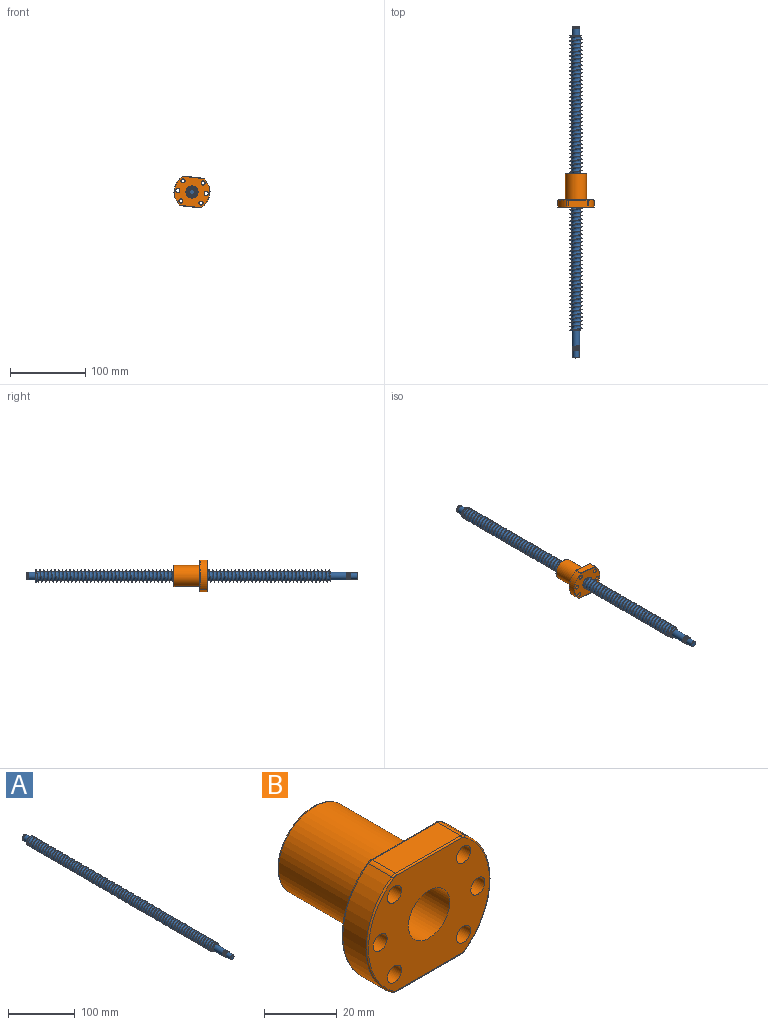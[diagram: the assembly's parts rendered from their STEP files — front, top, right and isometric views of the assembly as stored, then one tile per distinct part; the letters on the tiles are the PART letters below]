
ASSEMBLY  parts=2 mates=1
PART A: 29 faces, bbox 30.7x442.9x26.7 mm
  f0: cylinder r=5mm len=21mm, axis (0,1,0), area 629.1mm2, adj f1,f8,f9,f10,f18
  f1: cylinder r=5mm len=10mm, axis (0,1,0), area 1.6mm2, adj f0,f2,f9,f10
  f2: cylinder r=5mm len=10mm, axis (0,1,0), area 1.6mm2, adj f1,f3,f9,f10
  f3: cylinder r=5mm len=10mm, axis (0,1,0), area 1.6mm2, adj f2,f4,f9,f10
  f4: cylinder r=5mm len=10mm, axis (0,1,0), area 1.6mm2, adj f3,f5,f9,f10
  f5: cylinder r=5mm len=1.58mm, axis (0,1,0), area 0mm2, adj f4,f7,f9
  f6: plane 9.16x8.89mm, normal (0,-1,0), area 11.7mm2, adj f7,f9,f10,f20
  f7: cone r=4.5mm half-angle=45deg, axis (0,1,0), area 7mm2, adj f5,f6,f9,f10
  f8: plane 0.95x0.82mm, normal (-1,0,0), area 0.4mm2, adj f0,f9,f10
  f9: bspline ~11.55x10mm, area 140.3mm2, adj f0,f1,f2,f3,f4,f5,f6,f7
  f10: bspline ~11.55x10mm, area 153.7mm2, adj f0,f1,f2,f3,f4,f6,f7,f8
  f11: bspline ~399.07x29.85mm, area 24636.7mm2, adj f12,f13,f14,f15,f18,f19
  f12: plane 5.62x3.2mm, normal (-0.31,0,-0.95), area 9mm2, adj f11,f15,f19
  f13: cone r=7.03mm half-angle=45deg, axis (0,1,0), area 3.3mm2, adj f11,f18
  f14: cone r=7.03mm half-angle=45deg, axis (0,1,0), area 0.1mm2, adj f11,f19
  f15: cone r=8.02mm half-angle=45deg, axis (0,-1,0), area 60.9mm2, adj f11,f12,f17,f19
  f16: cylinder r=5mm len=10mm, axis (0,-1,0), area 282.7mm2, adj f17,f24
  f17: plane 14.05x14.05mm, normal (0,1,0), area 76.5mm2, adj f15,f16
  f18: plane 12.61x11.89mm, normal (0,-1,0), area 38.8mm2, adj f0,f11,f13
  f19: cylinder r=8.02mm len=392mm, axis (0,1,0), area 8085.4mm2, adj f11,f12,f14,f15
  f20: cylinder r=4mm len=10mm, axis (0,1,0), area 251.3mm2, adj f6,f22
  f21: plane 7x7mm, normal (0,-1,0), area 38.5mm2, adj f22
  f22: cone r=3.5mm half-angle=45deg, axis (0,1,0), area 16.7mm2, adj f20,f21
  f23: plane 10x10mm, normal (0,-1,0), area 6.2mm2, adj f25,f28
  f24: plane 10x10mm, normal (0,1,0), area 6.2mm2, adj f16,f25
  f25: cylinder r=4.8mm len=9.6mm, axis (0,-1,0), area 34.7mm2, adj f23,f24
  f26: plane 9x9mm, normal (0,1,0), area 63.6mm2, adj f27
  f27: cone r=5mm half-angle=45deg, axis (0,-1,0), area 21.1mm2, adj f26,f28
  f28: cylinder r=5mm len=10mm, axis (0,-1,0), area 42.4mm2, adj f23,f27
PART B: 37 faces, bbox 52x45x42 mm
  f0: cylinder r=14mm len=34mm, axis (0,-1,0), area 2990.8mm2, adj f35,f36
  f1: cylinder r=8.02mm len=45mm, axis (0,-1,0), area 2269mm2, adj f2,f3
  f2: plane 27x27mm, normal (0,1,0), area 370.2mm2, adj f1,f36
  f3: plane 47x38.77mm, normal (0,-1,0), area 1241.5mm2, adj f1,f7,f8,f9,f10,f11,f12,f27
  f4: plane 25.29x9mm, normal (0,0,1), area 227.6mm2, adj f15,f18,f25,f32
  f5: cylinder r=24mm len=38.82mm, axis (0,-1,0), area 406.9mm2, adj f15,f16,f24,f33
  f6: plane 25.29x9mm, normal (0,0,-1), area 227.6mm2, adj f16,f17,f20,f29
  f7: cylinder r=2.75mm len=10mm, axis (0,-1,0), area 172.8mm2, adj f3,f14
  f8: cylinder r=2.75mm len=10mm, axis (0,-1,0), area 172.8mm2, adj f3,f14
  f9: cylinder r=2.75mm len=10mm, axis (0,-1,0), area 172.8mm2, adj f3,f14
  f10: cylinder r=2.75mm len=10mm, axis (0,-1,0), area 172.8mm2, adj f3,f14
  f11: cylinder r=2.75mm len=10mm, axis (0,-1,0), area 172.8mm2, adj f3,f14
  f12: cylinder r=2.75mm len=10mm, axis (0,-1,0), area 172.8mm2, adj f3,f14
  f13: cylinder r=24mm len=38.82mm, axis (0,-1,0), area 406.9mm2, adj f17,f18,f21,f28
  f14: plane 47x38.77mm, normal (0,1,0), area 783.3mm2, adj f7,f8,f9,f10,f11,f12,f19,f20
  f15: cylinder r=2.5mm len=9mm, axis (0,-1,0), area 14.1mm2, adj f4,f5,f26,f34
  f16: cylinder r=2.5mm len=9mm, axis (0,-1,0), area 14.1mm2, adj f5,f6,f22,f31
  f17: cylinder r=2.5mm len=9mm, axis (0,-1,0), area 14.1mm2, adj f6,f13,f19,f27
  f18: cylinder r=2.5mm len=9mm, axis (0,-1,0), area 14.1mm2, adj f4,f13,f23,f30
  f19: torus R=2mm, axis (0,-1,0), area 1.1mm2, adj f14,f17,f20,f21
  f20: cylinder r=0.5mm len=25.29mm, axis (-1,0,0), area 19.9mm2, adj f6,f14,f19,f22
  f21: torus R=23.5mm, axis (0,-1,0), area 35.2mm2, adj f13,f14,f19,f23
  f22: torus R=2mm, axis (0,-1,0), area 1.1mm2, adj f14,f16,f20,f24
  f23: torus R=2mm, axis (0,-1,0), area 1.1mm2, adj f14,f18,f21,f25
  f24: torus R=23.5mm, axis (0,-1,0), area 35.2mm2, adj f5,f14,f22,f26
  f25: cylinder r=0.5mm len=25.29mm, axis (1,0,0), area 19.9mm2, adj f4,f14,f23,f26
  f26: torus R=2mm, axis (0,-1,0), area 1.1mm2, adj f14,f15,f24,f25
  f27: torus R=2mm, axis (0,-1,0), area 1.1mm2, adj f3,f17,f28,f29
  f28: torus R=23.5mm, axis (0,-1,0), area 35.2mm2, adj f3,f13,f27,f30
  f29: cylinder r=0.5mm len=25.29mm, axis (1,0,0), area 19.9mm2, adj f3,f6,f27,f31
  f30: torus R=2mm, axis (0,-1,0), area 1.1mm2, adj f3,f18,f28,f32
  f31: torus R=2mm, axis (0,-1,0), area 1.1mm2, adj f3,f16,f29,f33
  f32: cylinder r=0.5mm len=25.29mm, axis (-1,0,0), area 19.9mm2, adj f3,f4,f30,f34
  f33: torus R=23.5mm, axis (0,-1,0), area 35.2mm2, adj f3,f5,f31,f34
  f34: torus R=2mm, axis (0,-1,0), area 1.1mm2, adj f3,f15,f32,f33
  f35: torus R=14.5mm, axis (0,-1,0), area 70mm2, adj f0,f14
  f36: torus R=13.5mm, axis (0,-1,0), area 68.2mm2, adj f0,f2
PLACE A rot(axis=(0,-1,0),167deg) t=(13.32,-38.37,7.15)mm
PLACE B rot(axis=(0,-1,0),174deg) t=(13.32,-67.89,7.15)mm
MATE cylindrical B.f0 <-> A.f0  axis (0,-1,0) through (13.32,-67.89,7.15)mm
